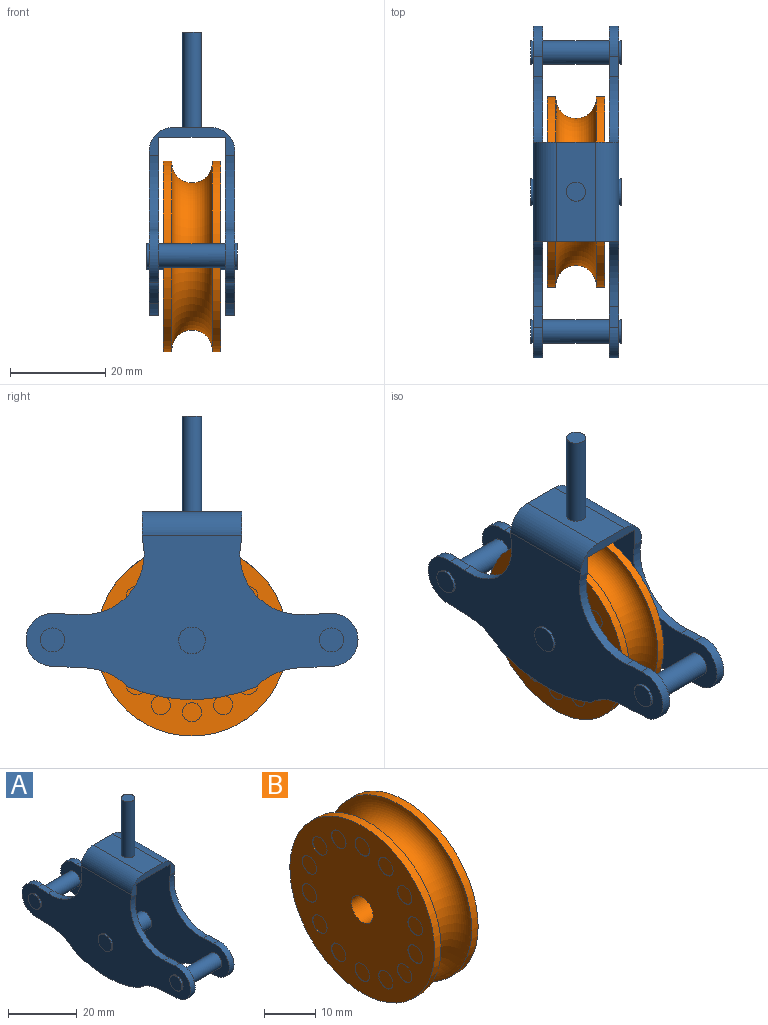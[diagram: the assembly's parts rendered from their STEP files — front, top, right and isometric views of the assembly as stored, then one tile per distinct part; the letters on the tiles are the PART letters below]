
ASSEMBLY  parts=2 mates=1
PART A: 49 faces, bbox 19x69.5x59.4 mm
  f0: cylinder r=5.55mm len=11.1mm, axis (-1,0,0), area 36.8mm2, adj f1,f13,f14,f15
  f1: plane 6.63x2mm, normal (0,-0.04,-1), area 13.3mm2, adj f0,f2,f14,f15
  f2: cylinder r=13.99mm len=9.28mm, axis (-1,0,0), area 20.7mm2, adj f1,f3,f14,f15
  f3: cylinder r=35.15mm len=26.56mm, axis (-1,0,0), area 54.5mm2, adj f2,f4,f14,f15
  f4: cylinder r=13.99mm len=9.28mm, axis (-1,0,0), area 20.7mm2, adj f3,f5,f14,f15
  f5: plane 6.63x2mm, normal (0,0.04,-1), area 13.3mm2, adj f4,f6,f14,f15
  f6: cylinder r=5.55mm len=11.1mm, axis (-1,0,0), area 36.8mm2, adj f5,f7,f14,f15
  f7: plane 4.19x2mm, normal (0,-0.03,1), area 8.4mm2, adj f6,f8,f14,f15
  f8: cylinder r=12.73mm len=15.75mm, axis (-1,0,0), area 48.8mm2, adj f7,f9,f14,f15
  f9: plane 18x5.88mm, normal (0,1,0), area 40.8mm2, adj f8,f10,f14,f15,f16,f25,f28,f29
  f10: plane 20.77x8mm, normal (0,0,1), area 153.6mm2, adj f9,f11,f30,f31,f48
  f11: plane 18x5.88mm, normal (0,-1,0), area 40.8mm2, adj f10,f12,f14,f15,f16,f26,f28,f29
  f12: cylinder r=12.73mm len=15.75mm, axis (-1,0,0), area 48.8mm2, adj f11,f13,f14,f15
  f13: plane 4.19x2mm, normal (0,0.03,1), area 8.4mm2, adj f0,f12,f14,f15
  f14: plane 69.54x34.39mm, normal (1,0,0), area 1264.6mm2, adj f0,f1,f2,f3,f4,f5,f6,f7
  f15: plane 69.54x37.39mm, normal (-1,0,0), area 1326.9mm2, adj f0,f1,f2,f3,f4,f5,f6,f7
  f16: plane 69.54x37.39mm, normal (1,0,0), area 1326.9mm2, adj f9,f11,f17,f18,f19,f20,f21,f22
  f17: cylinder r=5.55mm len=11.1mm, axis (1,0,0), area 36.8mm2, adj f16,f18,f27,f28
  f18: plane 6.63x2mm, normal (0,-0.04,-1), area 13.3mm2, adj f16,f17,f19,f28
  f19: cylinder r=13.99mm len=9.28mm, axis (1,0,0), area 20.7mm2, adj f16,f18,f20,f28
  f20: cylinder r=35.15mm len=26.56mm, axis (1,0,0), area 54.5mm2, adj f16,f19,f21,f28
  f21: cylinder r=13.99mm len=9.28mm, axis (1,0,0), area 20.7mm2, adj f16,f20,f22,f28
  f22: plane 6.63x2mm, normal (0,0.04,-1), area 13.3mm2, adj f16,f21,f23,f28
  f23: cylinder r=5.55mm len=11.1mm, axis (1,0,0), area 36.8mm2, adj f16,f22,f24,f28
  f24: plane 4.19x2mm, normal (0,-0.03,1), area 8.4mm2, adj f16,f23,f25,f28
  f25: cylinder r=12.73mm len=15.75mm, axis (1,0,0), area 48.8mm2, adj f9,f16,f24,f28
  f26: cylinder r=12.73mm len=15.75mm, axis (1,0,0), area 48.8mm2, adj f11,f16,f27,f28
  f27: plane 4.19x2mm, normal (0,0.03,1), area 8.4mm2, adj f16,f17,f26,f28
  f28: plane 69.54x34.39mm, normal (-1,0,0), area 1264.6mm2, adj f9,f11,f17,f18,f19,f20,f21,f22
  f29: plane 20.77x14mm, normal (0,0,-1), area 290.8mm2, adj f9,f11,f15,f16
  f30: cylinder r=5mm len=20.77mm, axis (0,1,0), area 163.2mm2, adj f9,f10,f11,f28
  f31: cylinder r=5mm len=20.77mm, axis (0,1,0), area 163.2mm2, adj f9,f10,f11,f14
  f32: plane 5x5mm, normal (-1,0,0), area 19.6mm2, adj f33
  f33: cylinder r=2.5mm len=5mm, axis (-1,0,0), area 7.9mm2, adj f28,f32
  f34: cylinder r=2.5mm len=14mm, axis (-1,0,0), area 219.9mm2, adj f15,f16
  f35: cylinder r=2.5mm len=5mm, axis (-1,0,0), area 7.9mm2, adj f14,f36
  f36: plane 5x5mm, normal (1,0,0), area 19.6mm2, adj f35
  f37: plane 5x5mm, normal (-1,0,0), area 19.6mm2, adj f38
  f38: cylinder r=2.5mm len=5mm, axis (-1,0,0), area 7.9mm2, adj f28,f37
  f39: cylinder r=2.5mm len=14mm, axis (-1,0,0), area 219.9mm2, adj f15,f16
  f40: cylinder r=2.5mm len=5mm, axis (-1,0,0), area 7.9mm2, adj f14,f41
  f41: plane 5x5mm, normal (1,0,0), area 19.6mm2, adj f40
  f42: plane 5.6x5.6mm, normal (-1,0,0), area 24.6mm2, adj f43
  f43: cylinder r=2.8mm len=5.6mm, axis (-1,0,0), area 8.8mm2, adj f28,f42
  f44: cylinder r=2.8mm len=14mm, axis (-1,0,0), area 246.3mm2, adj f15,f16
  f45: cylinder r=2.8mm len=5.6mm, axis (-1,0,0), area 8.8mm2, adj f14,f46
  f46: plane 5.6x5.6mm, normal (1,0,0), area 24.6mm2, adj f45
  f47: plane 4x4mm, normal (0,0,1), area 12.6mm2, adj f48
  f48: cylinder r=2mm len=20mm, axis (0,0,1), area 251.3mm2, adj f10,f47
PART B: 62 faces, bbox 12x49x49 mm
  f0: cylinder r=2mm len=4mm, axis (-1,0,0), area 1.3mm2, adj f1,f56
  f1: plane 4x4mm, normal (-1,0,0), area 12.6mm2, adj f0
  f2: cylinder r=2mm len=4mm, axis (-1,0,0), area 1.3mm2, adj f3,f56
  f3: plane 4x4mm, normal (-1,0,0), area 12.6mm2, adj f2
  f4: cylinder r=2mm len=4mm, axis (-1,0,0), area 1.3mm2, adj f5,f56
  f5: plane 4x4mm, normal (-1,0,0), area 12.6mm2, adj f4
  f6: cylinder r=2mm len=4mm, axis (-1,0,0), area 1.3mm2, adj f7,f56
  f7: plane 4x4mm, normal (-1,0,0), area 12.6mm2, adj f6
  f8: cylinder r=2mm len=4mm, axis (-1,0,0), area 1.3mm2, adj f9,f56
  f9: plane 4x4mm, normal (-1,0,0), area 12.6mm2, adj f8
  f10: cylinder r=2mm len=4mm, axis (-1,0,0), area 1.3mm2, adj f11,f56
  f11: plane 4x4mm, normal (-1,0,0), area 12.6mm2, adj f10
  f12: cylinder r=2mm len=4mm, axis (-1,0,0), area 1.3mm2, adj f13,f56
  f13: plane 4x4mm, normal (-1,0,0), area 12.6mm2, adj f12
  f14: cylinder r=2mm len=4mm, axis (-1,0,0), area 1.3mm2, adj f15,f56
  f15: plane 4x4mm, normal (-1,0,0), area 12.6mm2, adj f14
  f16: cylinder r=2mm len=4mm, axis (-1,0,0), area 1.3mm2, adj f17,f56
  f17: plane 4x4mm, normal (-1,0,0), area 12.6mm2, adj f16
  f18: cylinder r=2mm len=4mm, axis (-1,0,0), area 1.3mm2, adj f19,f56
  f19: plane 4x4mm, normal (-1,0,0), area 12.6mm2, adj f18
  f20: cylinder r=2mm len=4mm, axis (-1,0,0), area 1.3mm2, adj f21,f56
  f21: plane 4x4mm, normal (-1,0,0), area 12.6mm2, adj f20
  f22: cylinder r=2mm len=4mm, axis (-1,0,0), area 1.3mm2, adj f23,f56
  f23: plane 4x4mm, normal (-1,0,0), area 12.6mm2, adj f22
  f24: cylinder r=2mm len=4mm, axis (-1,0,0), area 1.3mm2, adj f25,f56
  f25: plane 4x4mm, normal (-1,0,0), area 12.6mm2, adj f24
  f26: cylinder r=2mm len=4mm, axis (1,0,0), area 1.3mm2, adj f27,f55
  f27: plane 4x4mm, normal (1,0,0), area 12.6mm2, adj f26
  f28: cylinder r=2mm len=4mm, axis (1,0,0), area 1.3mm2, adj f29,f55
  f29: plane 4x4mm, normal (1,0,0), area 12.6mm2, adj f28
  f30: cylinder r=2mm len=4mm, axis (1,0,0), area 1.3mm2, adj f31,f55
  f31: plane 4x4mm, normal (1,0,0), area 12.6mm2, adj f30
  f32: cylinder r=2mm len=4mm, axis (1,0,0), area 1.3mm2, adj f33,f55
  f33: plane 4x4mm, normal (1,0,0), area 12.6mm2, adj f32
  f34: cylinder r=2mm len=4mm, axis (1,0,0), area 1.3mm2, adj f35,f55
  f35: plane 4x4mm, normal (1,0,0), area 12.6mm2, adj f34
  f36: cylinder r=2mm len=4mm, axis (1,0,0), area 1.3mm2, adj f37,f55
  f37: plane 4x4mm, normal (1,0,0), area 12.6mm2, adj f36
  f38: cylinder r=2mm len=4mm, axis (1,0,0), area 1.3mm2, adj f39,f55
  f39: plane 4x4mm, normal (1,0,0), area 12.6mm2, adj f38
  f40: cylinder r=2mm len=4mm, axis (1,0,0), area 1.3mm2, adj f41,f55
  f41: plane 4x4mm, normal (1,0,0), area 12.6mm2, adj f40
  f42: cylinder r=2mm len=4mm, axis (1,0,0), area 1.3mm2, adj f43,f55
  f43: plane 4x4mm, normal (1,0,0), area 12.6mm2, adj f42
  f44: cylinder r=2mm len=4mm, axis (1,0,0), area 1.3mm2, adj f45,f55
  f45: plane 4x4mm, normal (1,0,0), area 12.6mm2, adj f44
  f46: cylinder r=2mm len=4mm, axis (1,0,0), area 1.3mm2, adj f47,f55
  f47: plane 4x4mm, normal (1,0,0), area 12.6mm2, adj f46
  f48: cylinder r=2mm len=4mm, axis (1,0,0), area 1.3mm2, adj f49,f55
  f49: plane 4x4mm, normal (1,0,0), area 12.6mm2, adj f48
  f50: cylinder r=2mm len=4mm, axis (1,0,0), area 1.3mm2, adj f51,f55
  f51: plane 4x4mm, normal (1,0,0), area 12.6mm2, adj f50
  f52: cylinder r=20mm len=40mm, axis (-1,0,0), area 222.6mm2, adj f55,f57
  f53: cylinder r=3mm len=12mm, axis (-1,0,0), area 226.2mm2, adj f55,f56
  f54: cylinder r=20mm len=40mm, axis (-1,0,0), area 222.6mm2, adj f56,f57
  f55: plane 40x40mm, normal (1,0,0), area 1052.4mm2, adj f26,f28,f30,f32,f34,f36,f38,f40
  f56: plane 40x40mm, normal (-1,0,0), area 1052.4mm2, adj f0,f2,f4,f6,f8,f10,f12,f14
  f57: torus R=19.64mm, axis (1,0,0), area 1508.2mm2, adj f52,f54
  f58: cylinder r=2mm len=4mm, axis (1,0,0), area 1.3mm2, adj f55,f59
  f59: plane 4x4mm, normal (1,0,0), area 12.6mm2, adj f58
  f60: cylinder r=2mm len=4mm, axis (-1,0,0), area 1.3mm2, adj f56,f61
  f61: plane 4x4mm, normal (-1,0,0), area 12.6mm2, adj f60
PLACE A at identity fixed
PLACE B at identity
MATE revolute B.f52 <-> A.f43  axis (-1,0,0) through (-6,0,-21.14)mm
